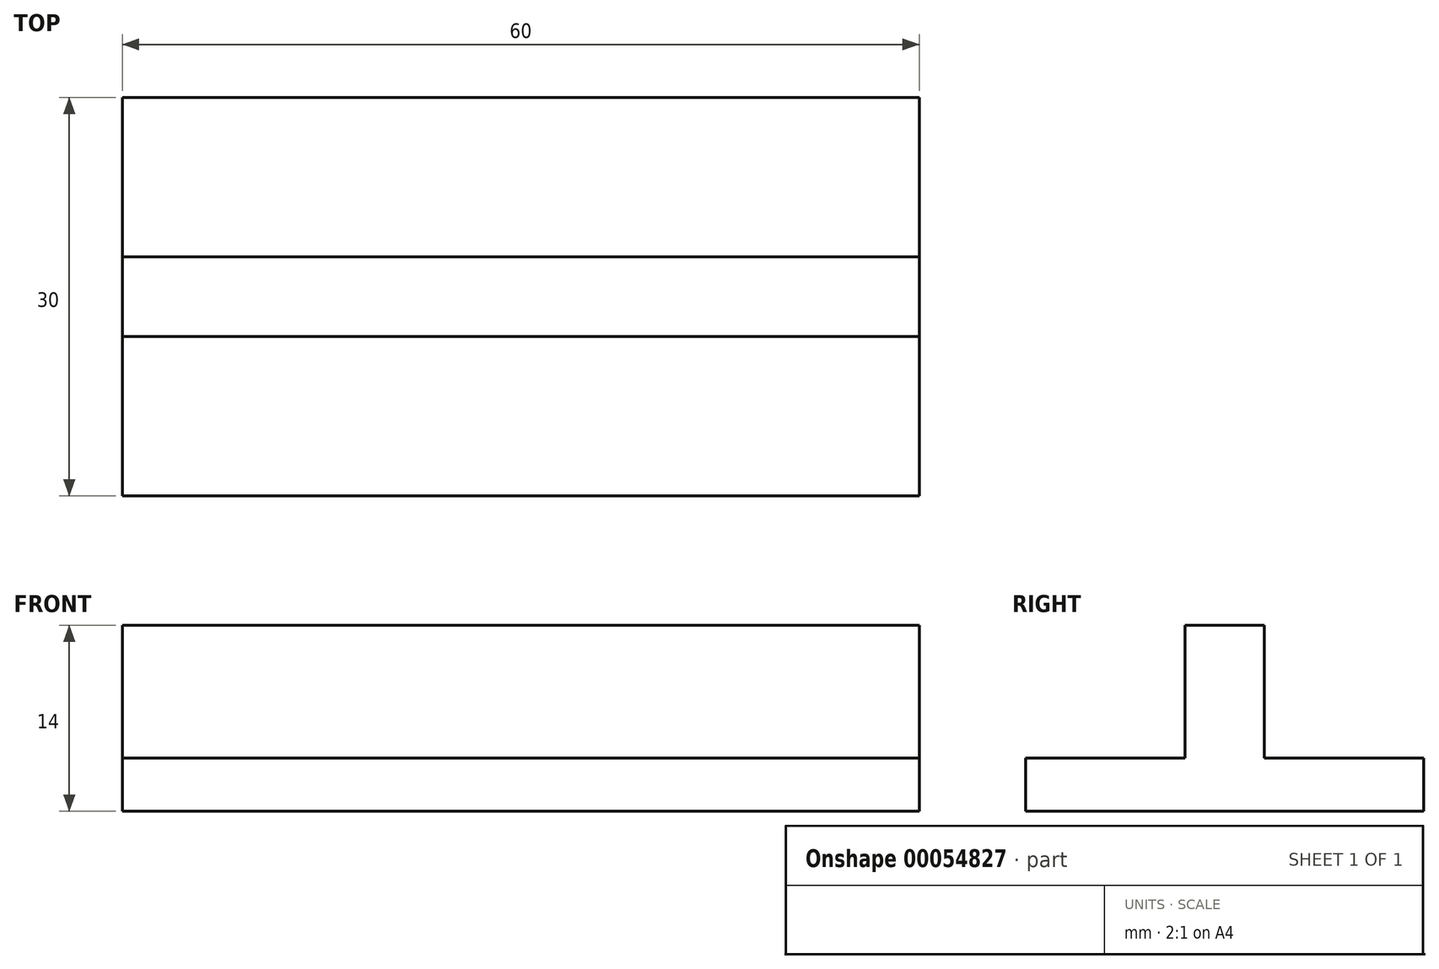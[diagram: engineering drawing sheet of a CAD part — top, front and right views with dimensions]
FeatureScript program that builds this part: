
annotation { "Feature Type Name" : "Feature", "Feature Type Description" : "" }
export const myFeature = defineFeature(function(context is Context, id is Id, definition is map)
    precondition{}
    {
        {
            var Q0;
            Q0=qCreatedBy(makeId("Top.planeOp"),FACE);
            var sketch = newSketch(context, id + "F0", { "sketchPlane" : qUnion([Q0])});
            skLineSegment(sketch, "E0.rect.bottom", {"start": v(30, 15) * mm, "end": v(-30, 15) * mm});
            skLineSegment(sketch, "E0.rect.top", {"start": v(30, -15) * mm, "end": v(-30, -15) * mm});
            skLineSegment(sketch, "E0.rect.left", {"start": v(30, 15) * mm, "end": v(30, -15) * mm});
            skLineSegment(sketch, "E0.rect.right", {"start": v(-30, 15) * mm, "end": v(-30, -15) * mm});
            skPoint(sketch, "E0.rect.middle", {"position": v(0, 0) * mm});
            skSolve(sketch);
        }
        {
            var Q0;
            Q0=makeQuery(id+"F0.imprint","IMPRINT",FACE,{"disambiguationData":[TD([[makeQuery(id+"F0.imprint","IMPRINT",EDGE,{"derivedFrom":sQuery(id+"F0.wireOp",EDGE,"E0.rect.bottom")}),1.0]])]});
            extrude(context, id + "F1", {"entities" : qUnion([Q0]), "depth" : 4 * mm});
        }
        {
            var Q0;
            Q0=makeQuery(id+"F1.opExtrude","CAP_FACE",FACE,{"disambiguationData":[OSD([sQuery(id+"F0.wireOp",EDGE,"E0.rect.bottom"),sQuery(id+"F0.wireOp",EDGE,"E0.rect.top"),sQuery(id+"F0.wireOp",EDGE,"E0.rect.left"),sQuery(id+"F0.wireOp",EDGE,"E0.rect.right")])],"isStart":false});
            var sketch = newSketch(context, id + "F2", { "sketchPlane" : qUnion([Q0])});
            skLineSegment(sketch, "E1.rect.bottom", {"start": v(30, 3) * mm, "end": v(-30, 3) * mm});
            skLineSegment(sketch, "E1.rect.top", {"start": v(30, -3) * mm, "end": v(-30, -3) * mm});
            skLineSegment(sketch, "E1.rect.left", {"start": v(30, 3) * mm, "end": v(30, -3) * mm});
            skLineSegment(sketch, "E1.rect.right", {"start": v(-30, 3) * mm, "end": v(-30, -3) * mm});
            skPoint(sketch, "E1.rect.middle", {"position": v(0, 0) * mm});
            skSolve(sketch);
        }
        {
            var Q0;
            Q0=makeQuery(id+"F2.imprint","IMPRINT",FACE,{"disambiguationData":[TD([[makeQuery(id+"F2.imprint","IMPRINT",EDGE,{"derivedFrom":sQuery(id+"F2.wireOp",EDGE,"E1.rect.bottom")}),1.0]])]});
            extrude(context, id + "F3", {"entities" : qUnion([Q0]), "operationType" : NewBodyOperationType.ADD, "depth" : 10 * mm});
        }
    });
